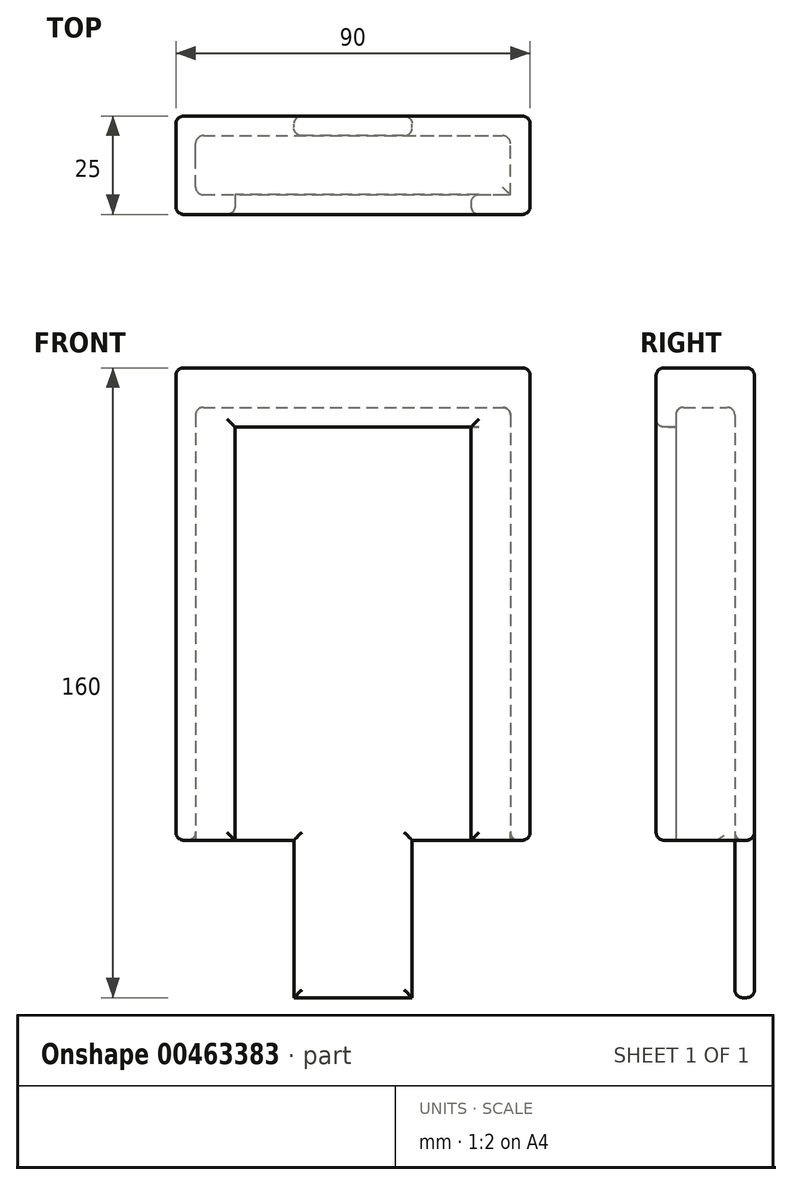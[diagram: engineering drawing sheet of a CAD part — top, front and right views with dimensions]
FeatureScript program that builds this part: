
annotation { "Feature Type Name" : "Feature", "Feature Type Description" : "" }
export const myFeature = defineFeature(function(context is Context, id is Id, definition is map)
    precondition{}
    {
        {
            var Q0;
            Q0=qCreatedBy(makeId("Top.planeOp"),FACE);
            var sketch = newSketch(context, id + "F0", { "sketchPlane" : qUnion([Q0])});
            skLineSegment(sketch, "E0.bottom", {"start": v(-45, -12.5) * mm, "end": v(45, -12.5) * mm});
            skLineSegment(sketch, "E0.top", {"start": v(-45, 12.5) * mm, "end": v(45, 12.5) * mm});
            skLineSegment(sketch, "E0.left", {"start": v(-45, -12.5) * mm, "end": v(-45, 12.5) * mm});
            skLineSegment(sketch, "E0.right", {"start": v(45, -12.5) * mm, "end": v(45, 12.5) * mm});
            skPoint(sketch, "E0.middle", {"position": v(0, 0) * mm});
            skLineSegment(sketch, "E1.bottom", {"start": v(-40, -7.5) * mm, "end": v(40, -7.5) * mm});
            skLineSegment(sketch, "E1.top", {"start": v(-40, 7.5) * mm, "end": v(40, 7.5) * mm});
            skLineSegment(sketch, "E1.left", {"start": v(-40, -7.5) * mm, "end": v(-40, 7.5) * mm});
            skLineSegment(sketch, "E1.right", {"start": v(40, -7.5) * mm, "end": v(40, 7.5) * mm});
            skSolve(sketch);
        }
        {
            var Q0;
            Q0=makeQuery(id+"F0.imprint","IMPRINT",FACE,{"disambiguationData":[TD([[makeQuery(id+"F0.imprint","IMPRINT",EDGE,{"derivedFrom":sQuery(id+"F0.wireOp",EDGE,"E0.bottom")}),1.0]])]});
            var Q1;
            Q1=makeQuery(id+"F0.imprint","IMPRINT",FACE,{"disambiguationData":[TD([[makeQuery(id+"F0.imprint","IMPRINT",EDGE,{"derivedFrom":sQuery(id+"F0.wireOp",EDGE,"E1.bottom")}),1.0]])]});
            extrude(context, id + "F1", {"entities" : qUnion([Q0, Q1]), "depth" : 120 * mm});
        }
        {
            var Q0;
            Q0=makeQuery(id+"F1.opExtrude","SWEPT_FACE",FACE,{"disambiguationData":[OSD([sQuery(id+"F0.wireOp",EDGE,"E0.bottom")])]});
            var sketch = newSketch(context, id + "F2", { "sketchPlane" : qUnion([Q0])});
            skLineSegment(sketch, "E2.bottom", {"start": v(-30, 0) * mm, "end": v(30, 0) * mm});
            skLineSegment(sketch, "E2.top", {"start": v(-30, 105) * mm, "end": v(30, 105) * mm});
            skLineSegment(sketch, "E2.left", {"start": v(-30, 0) * mm, "end": v(-30, 105) * mm});
            skLineSegment(sketch, "E2.right", {"start": v(30, 0) * mm, "end": v(30, 105) * mm});
            skSolve(sketch);
        }
        {
            var Q0;
            Q0=makeQuery(id+"F0.imprint","IMPRINT",FACE,{"disambiguationData":[TD([[makeQuery(id+"F0.imprint","IMPRINT",EDGE,{"derivedFrom":sQuery(id+"F0.wireOp",EDGE,"E1.bottom")}),1.0]])]});
            extrude(context, id + "F3", {"entities" : qUnion([Q0]), "operationType" : NewBodyOperationType.REMOVE, "depth" : 110 * mm});
        }
        {
            var Q0;
            Q0=makeQuery(id+"F2.imprint","IMPRINT",FACE,{"disambiguationData":[TD([[makeQuery(id+"F2.imprint","IMPRINT",EDGE,{"derivedFrom":sQuery(id+"F2.wireOp",EDGE,"E2.bottom")}),1.0]])]});
            extrude(context, id + "F4", {"entities" : qUnion([Q0]), "operationType" : NewBodyOperationType.REMOVE, "oppositeDirection" : true, "depth" : 10 * mm});
        }
        {
            var Q0;
            Q0=makeQuery(id+"F1.opExtrude","SWEPT_FACE",FACE,{"disambiguationData":[OSD([sQuery(id+"F0.wireOp",EDGE,"E0.top")])]});
            var sketch = newSketch(context, id + "F5", { "sketchPlane" : qUnion([Q0])});
            skLineSegment(sketch, "E3.bottom", {"start": v(-15, 0) * mm, "end": v(15, 0) * mm});
            skLineSegment(sketch, "E3.top", {"start": v(-15, -40) * mm, "end": v(15, -40) * mm});
            skLineSegment(sketch, "E3.left", {"start": v(-15, 0) * mm, "end": v(-15, -40) * mm});
            skLineSegment(sketch, "E3.right", {"start": v(15, 0) * mm, "end": v(15, -40) * mm});
            skSolve(sketch);
        }
        {
            var Q0;
            Q0=makeQuery(id+"F5.imprint","IMPRINT",FACE,{"disambiguationData":[TD([[makeQuery(id+"F5.imprint","IMPRINT",EDGE,{"derivedFrom":sQuery(id+"F5.wireOp",EDGE,"E3.bottom")}),1.0]])]});
            extrude(context, id + "F6", {"entities" : qUnion([Q0]), "operationType" : NewBodyOperationType.ADD, "oppositeDirection" : true, "depth" : 5 * mm});
        }
        {
            var Q0;
            Q0=makeQuery(id+"F6.boolean.opBoolean","MERGE",FACE,{"derivedFrom":[makeQuery(id+"F3.boolean.opBoolean","COPY",FACE,{"derivedFrom":makeQuery(id+"F3.opExtrude","SWEPT_FACE",FACE,{"disambiguationData":[OSD([sQuery(id+"F0.wireOp",EDGE,"E1.top")])]})}),makeQuery(id+"F6.opExtrude","CAP_FACE",FACE,{"disambiguationData":[OSD([sQuery(id+"F5.wireOp",EDGE,"E3.bottom"),sQuery(id+"F5.wireOp",EDGE,"E3.top"),sQuery(id+"F5.wireOp",EDGE,"E3.left"),sQuery(id+"F5.wireOp",EDGE,"E3.right")])],"isStart":false})]});
            var Q1;
            Q1=makeQuery(id+"F4.boolean.opBoolean","INTERSECT",EDGE,{"derivedFrom":[makeQuery(id+"F3.boolean.opBoolean","COPY",FACE,{"derivedFrom":makeQuery(id+"F3.opExtrude","SWEPT_FACE",FACE,{"disambiguationData":[OSD([sQuery(id+"F0.wireOp",EDGE,"E1.bottom")])]})}),makeQuery(id+"F4.opExtrude","SWEPT_FACE",FACE,{"disambiguationData":[OSD([sQuery(id+"F2.wireOp",EDGE,"E2.right")])]})]});
            var Q2;
            Q2=makeQuery(id+"F3.boolean.opBoolean","COPY",EDGE,{"derivedFrom":makeQuery(id+"F3.opExtrude","SWEPT_EDGE",EDGE,{"disambiguationData":[OSD([sQuery(id+"F0.wireOp",EDGE,"E1.bottom"),sQuery(id+"F0.wireOp",EDGE,"E1.left")])]})});
            var Q3;
            Q3=makeQuery(id+"F3.boolean.opBoolean","COPY",FACE,{"derivedFrom":makeQuery(id+"F3.opExtrude","CAP_FACE",FACE,{"disambiguationData":[OSD([sQuery(id+"F0.wireOp",EDGE,"E1.bottom"),sQuery(id+"F0.wireOp",EDGE,"E1.top"),sQuery(id+"F0.wireOp",EDGE,"E1.left"),sQuery(id+"F0.wireOp",EDGE,"E1.right")])],"isStart":false})});
            var Q4;
            Q4=makeQuery(id+"F1.opExtrude","SWEPT_FACE",FACE,{"disambiguationData":[OSD([sQuery(id+"F0.wireOp",EDGE,"E0.bottom")])]});
            var Q5;
            Q5=makeQuery(id+"F1.opExtrude","SWEPT_FACE",FACE,{"disambiguationData":[OSD([sQuery(id+"F0.wireOp",EDGE,"E0.right")])]});
            var Q6;
            Q6=makeQuery(id+"F6.boolean.opBoolean","MERGE",FACE,{"derivedFrom":[makeQuery(id+"F1.opExtrude","SWEPT_FACE",FACE,{"disambiguationData":[OSD([sQuery(id+"F0.wireOp",EDGE,"E0.top")])]}),makeQuery(id+"F6.opExtrude","CAP_FACE",FACE,{"disambiguationData":[OSD([sQuery(id+"F5.wireOp",EDGE,"E3.bottom"),sQuery(id+"F5.wireOp",EDGE,"E3.top"),sQuery(id+"F5.wireOp",EDGE,"E3.left"),sQuery(id+"F5.wireOp",EDGE,"E3.right")])],"isStart":true})]});
            var Q7;
            Q7=makeQuery(id+"F1.opExtrude","SWEPT_FACE",FACE,{"disambiguationData":[OSD([sQuery(id+"F0.wireOp",EDGE,"E0.left")])]});
            var Q8;
            Q8=makeQuery(id+"F1.opExtrude","CAP_FACE",FACE,{"disambiguationData":[OSD([sQuery(id+"F0.wireOp",EDGE,"E0.bottom"),sQuery(id+"F0.wireOp",EDGE,"E0.top"),sQuery(id+"F0.wireOp",EDGE,"E0.left"),sQuery(id+"F0.wireOp",EDGE,"E0.right")])],"isStart":false});
            fillet(context, id + "F7", {"entities" : qUnion([Q0, Q1, Q2, Q3, Q4, Q5, Q6, Q7, Q8]), "radius" : 2 * mm, "tangentPropagation" : true, "allowEdgeOverflow" : false});
        }
    });
